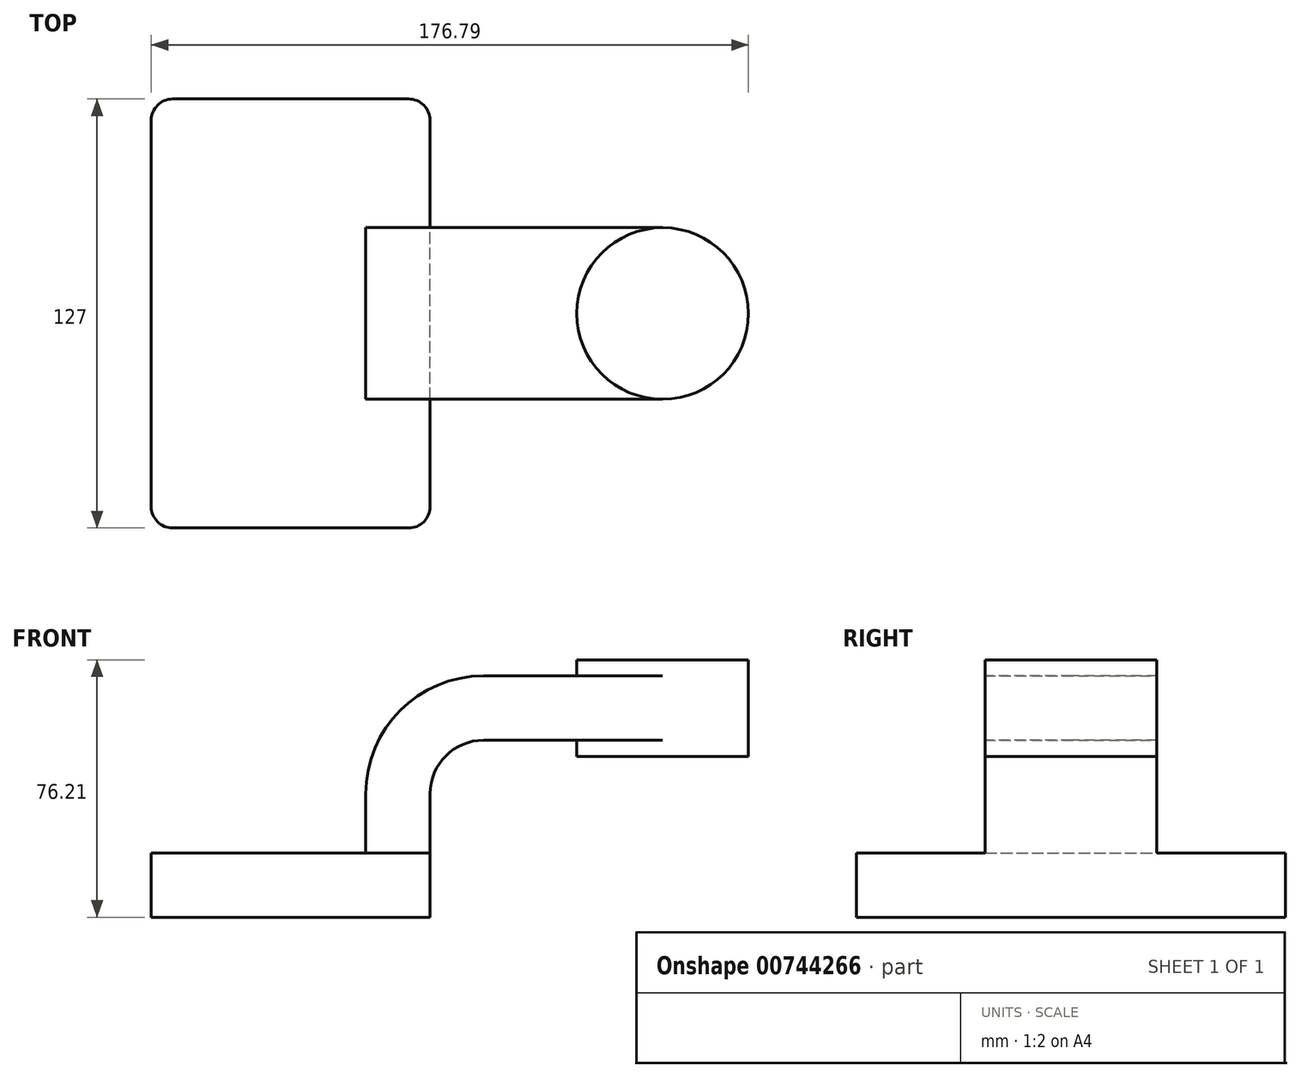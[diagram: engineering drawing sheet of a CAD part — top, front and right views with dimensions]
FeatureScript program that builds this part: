
annotation { "Feature Type Name" : "Feature", "Feature Type Description" : "" }
export const myFeature = defineFeature(function(context is Context, id is Id, definition is map)
    precondition{}
    {
        {
            var Q0;
            Q0=qCreatedBy(makeId("Front.planeOp"),FACE);
            var sketch = newSketch(context, id + "F0", { "sketchPlane" : qUnion([Q0])});
            skLineSegment(sketch, "E0.bottom", {"start": v(41.27, 9.53) * mm, "end": v(-41.28, 9.53) * mm});
            skLineSegment(sketch, "E0.top", {"start": v(41.28, -9.52) * mm, "end": v(-41.27, -9.52) * mm});
            skLineSegment(sketch, "E0.left", {"start": v(41.28, 9.53) * mm, "end": v(41.28, -9.52) * mm});
            skLineSegment(sketch, "E0.right", {"start": v(-41.28, 9.53) * mm, "end": v(-41.27, -9.52) * mm});
            skPoint(sketch, "E0.middle", {"position": v(0, 0) * mm});
            skLineSegment(sketch, "E1.bottom", {"start": v(135.52, 66.68) * mm, "end": v(84.72, 66.68) * mm});
            skLineSegment(sketch, "E1.top", {"start": v(135.52, 38.1) * mm, "end": v(84.72, 38.1) * mm});
            skLineSegment(sketch, "E1.left", {"start": v(135.52, 66.68) * mm, "end": v(135.52, 38.1) * mm});
            skLineSegment(sketch, "E1.right", {"start": v(84.72, 66.68) * mm, "end": v(84.72, 38.1) * mm});
            skPoint(sketch, "E1.middle", {"position": v(110.12, 52.39) * mm});
            skLineSegment(sketch, "E2", {"start": v(41.27, 9.53) * mm, "end": v(41.27, 27) * mm});
            skArc(sketch, "E3", {"start": v(41.27, 27) * mm, "mid": v(45.92, 38.23) * mm, "end": v(57.15, 42.88) * mm});
            skLineSegment(sketch, "E4", {"start": v(57.15, 42.88) * mm, "end": v(110.12, 42.88) * mm});
            skPoint(sketch, "E4.endSnap0", {"position": v(110.12, 38.1) * mm});
            skLineSegment(sketch, "E5.0", {"start": v(57.15, 61.93) * mm, "end": v(110.12, 61.93) * mm});
            skArc(sketch, "E5.1", {"start": v(22.22, 27) * mm, "mid": v(32.45, 51.7) * mm, "end": v(57.15, 61.93) * mm});
            skLineSegment(sketch, "E5.2", {"start": v(22.22, 9.53) * mm, "end": v(22.22, 27) * mm});
            skLineSegment(sketch, "E6", {"start": v(110.12, 38.1) * mm, "end": v(110.12, 66.68) * mm});
            skFitSpline(sketch, "E7", {"points": [v(-41.28, 9.52) * mm, v(57.15, 61.93) * mm], "startDerivative": vector(27.97, 95.31) * mm, "endDerivative": vector(122.54, -6.37) * mm});
            skSolve(sketch);
        }
        {
            var Q0;
            Q0=makeQuery(id+"F0.imprint","IMPRINT",FACE,{"disambiguationData":[TD([[makeQuery(id+"F0.imprint","IMPRINT",EDGE,{"derivedFrom":sQuery(id+"F0.wireOp",EDGE,"E0.top")}),-1.0]])]});
            extrude(context, id + "F1", {"entities" : qUnion([Q0]), "endBound" : BoundingType.SYMMETRIC, "depth" : 127 * mm, "offsetDistance" : 25.4 * mm});
        }
        {
            var Q0;
            {var subQ1=sQuery(id+"F0.wireOp",EDGE,"E2");Q0=makeQuery(id+"F0.imprint","IMPRINT",FACE,{"disambiguationData":[TD([[makeQuery(id+"F0.imprint","IMPRINT",EDGE,{"derivedFrom":subQ1}),1.0]])]});}
            extrude(context, id + "F2", {"entities" : qUnion([Q0]), "operationType" : NewBodyOperationType.ADD, "endBound" : BoundingType.SYMMETRIC, "depth" : 50.8 * mm, "offsetDistance" : 25.4 * mm});
        }
        {
            var Q0;
            Q0=makeQuery(id+"F0.imprint","IMPRINT",FACE,{"disambiguationData":[TD([[makeQuery(id+"F0.imprint","IMPRINT",EDGE,{"derivedFrom":sQuery(id+"F0.wireOp",EDGE,"E5.1")}),1.0]])]});
            extrude(context, id + "F3", {"entities" : qUnion([Q0]), "operationType" : NewBodyOperationType.ADD, "endBound" : BoundingType.SYMMETRIC, "depth" : 15.88 * mm, "offsetDistance" : 25.4 * mm});
        }
        {
            var Q0;
            {var subQ0=sQuery(id+"F0.wireOp",EDGE,"E5.0");var subQ1=sQuery(id+"F0.wireOp",EDGE,"E1.right");var subQ2=makeQuery(id+"F0.imprint","INTERSECT",VERTEX,{"derivedFrom":[subQ1,subQ0]});Q0=makeQuery(id+"F0.imprint","IMPRINT",FACE,{"disambiguationData":[TD([[makeQuery(id+"F0.imprint","IMPRINT",EDGE,{"disambiguationData":[TD([[subQ2,-1.0]])],"derivedFrom":subQ1}),1.0]])]});}
            extrude(context, id + "F4", {"entities" : qUnion([Q0]), "operationType" : NewBodyOperationType.ADD, "endBound" : BoundingType.SYMMETRIC, "depth" : 50.8 * mm, "offsetDistance" : 25.4 * mm});
        }
        {
            var Q0;
            {var subQ4=sQuery(id+"F0.wireOp",EDGE,"E1.left");Q0=makeQuery(id+"F0.imprint","IMPRINT",FACE,{"disambiguationData":[TD([[makeQuery(id+"F0.imprint","IMPRINT",EDGE,{"derivedFrom":subQ4}),-1.0]])]});}
            var Q1;
            Q1=sQuery(id+"F0.wireOp",EDGE,"E6");
            revolve(context, id + "F5", {"operationType" : NewBodyOperationType.ADD, "surfaceOperationType" : NewSurfaceOperationType.NEW, "entities" : qUnion([Q0]), "axis" : qUnion([Q1]), "revolveType" : RevolveType.FULL});
        }
        {
            var Q0;
            Q0=makeQuery(id+"F1.opExtrude","CAP_EDGE",EDGE,{"disambiguationData":[OSD([sQuery(id+"F0.wireOp",EDGE,"E0.right")])],"isStart":false});
            var Q1;
            Q1=makeQuery(id+"F1.opExtrude","CAP_EDGE",EDGE,{"disambiguationData":[OSD([sQuery(id+"F0.wireOp",EDGE,"E0.left")])],"isStart":false});
            var Q2;
            Q2=makeQuery(id+"F1.opExtrude","CAP_EDGE",EDGE,{"disambiguationData":[OSD([sQuery(id+"F0.wireOp",EDGE,"E0.left")])],"isStart":true});
            var Q3;
            Q3=makeQuery(id+"F1.opExtrude","CAP_EDGE",EDGE,{"disambiguationData":[OSD([sQuery(id+"F0.wireOp",EDGE,"E0.right")])],"isStart":true});
            fillet(context, id + "F6", {"entities" : qUnion([Q0, Q1, Q2, Q3]), "radius" : 6.35 * mm, "tangentPropagation" : true, "allowEdgeOverflow" : false});
        }
    });
